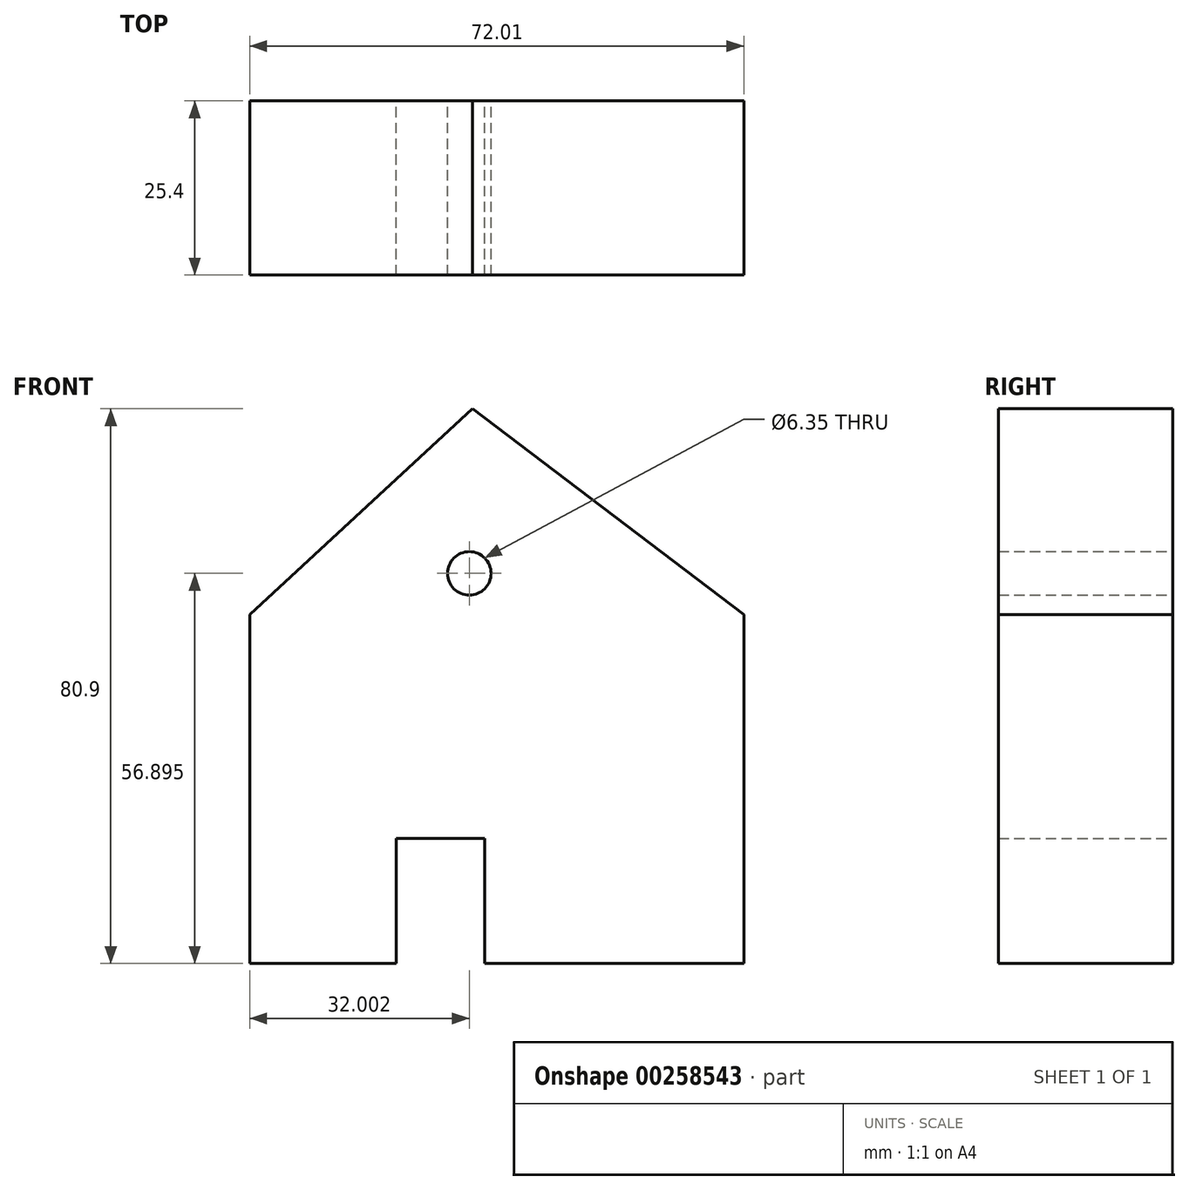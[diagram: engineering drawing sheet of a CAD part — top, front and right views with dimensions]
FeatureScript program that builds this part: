
annotation { "Feature Type Name" : "Feature", "Feature Type Description" : "" }
export const myFeature = defineFeature(function(context is Context, id is Id, definition is map)
    precondition{}
    {
        {
            var Q0;
            Q0=qCreatedBy(makeId("Front.planeOp"),FACE);
            var sketch = newSketch(context, id + "F0", { "sketchPlane" : qUnion([Q0])});
            skLineSegment(sketch, "E0.bottom", {"start": v(-24.9, 20.22) * mm, "end": v(47.12, 20.22) * mm});
            skLineSegment(sketch, "E0.top", {"start": v(-24.9, -30.67) * mm, "end": v(47.12, -30.67) * mm});
            skLineSegment(sketch, "E0.left", {"start": v(-24.9, 20.22) * mm, "end": v(-24.9, -30.67) * mm});
            skLineSegment(sketch, "E0.right", {"start": v(47.12, 20.22) * mm, "end": v(47.12, -30.67) * mm});
            skLineSegment(sketch, "E1", {"start": v(-24.9, 20.22) * mm, "end": v(7.56, 50.23) * mm});
            skLineSegment(sketch, "E2", {"start": v(7.56, 50.23) * mm, "end": v(47.12, 20.22) * mm});
            skLineSegment(sketch, "E3", {"start": v(-3.56, -30.67) * mm, "end": v(-3.56, -12.45) * mm});
            skLineSegment(sketch, "E4", {"start": v(-3.56, -12.45) * mm, "end": v(9.33, -12.45) * mm});
            skLineSegment(sketch, "E5", {"start": v(9.33, -12.45) * mm, "end": v(9.33, -30.67) * mm});
            skSolve(sketch);
        }
        {
            var Q0;
            Q0=makeQuery(id+"F0.imprint","IMPRINT",FACE,{"disambiguationData":[TD([[makeQuery(id+"F0.imprint","IMPRINT",EDGE,{"derivedFrom":sQuery(id+"F0.wireOp",EDGE,"E0.bottom")}),1.0]])]});
            var Q1;
            Q1=makeQuery(id+"F0.imprint","IMPRINT",FACE,{"disambiguationData":[TD([[makeQuery(id+"F0.imprint","IMPRINT",EDGE,{"derivedFrom":sQuery(id+"F0.wireOp",EDGE,"E0.bottom")}),-1.0]])]});
            extrude(context, id + "F1", {"entities" : qUnion([Q0, Q1]), "depth" : 25.4 * mm});
        }
        {
            var Q0;
            Q0=qCreatedBy(makeId("Front.planeOp"),FACE);
            var sketch = newSketch(context, id + "F2", { "sketchPlane" : qUnion([Q0])});
            skCircle(sketch, "E6", {"center": v(28.45, 0) * mm, "radius": 9.46 * mm});
            skCircle(sketch, "E7", {"center": v(7.11, 26.23) * mm, "radius": 8.05 * mm});
            skSolve(sketch);
        }
        {
            var Q0;
            Q0=sQuery(id+"F2.wireOp",VERTEX,"E7.center");
            var Q1;
            Q1=makeQuery(id+"F1.opExtrude","SWEPT_BODY",BODY,{"disambiguationData":[OSD([sQuery(id+"F0.wireOp",EDGE,"E0.top"),sQuery(id+"F0.wireOp",EDGE,"E0.left"),sQuery(id+"F0.wireOp",EDGE,"E0.right"),sQuery(id+"F0.wireOp",EDGE,"E1"),sQuery(id+"F0.wireOp",EDGE,"E2"),sQuery(id+"F0.wireOp",EDGE,"E3"),sQuery(id+"F0.wireOp",EDGE,"E4"),sQuery(id+"F0.wireOp",EDGE,"E5")])]});
            hole(context, id + "F3", {"style" : HoleStyle.SIMPLE, "endStyle" : HoleEndStyle.THROUGH, "oppositeDirection" : true, "holeDiameter" : 6.35 * mm, "tappedDepth" : 12.7 * mm, "tapClearance" : 3, "locations" : qUnion([Q0]), "scope" : qUnion([Q1])});
        }
    });
